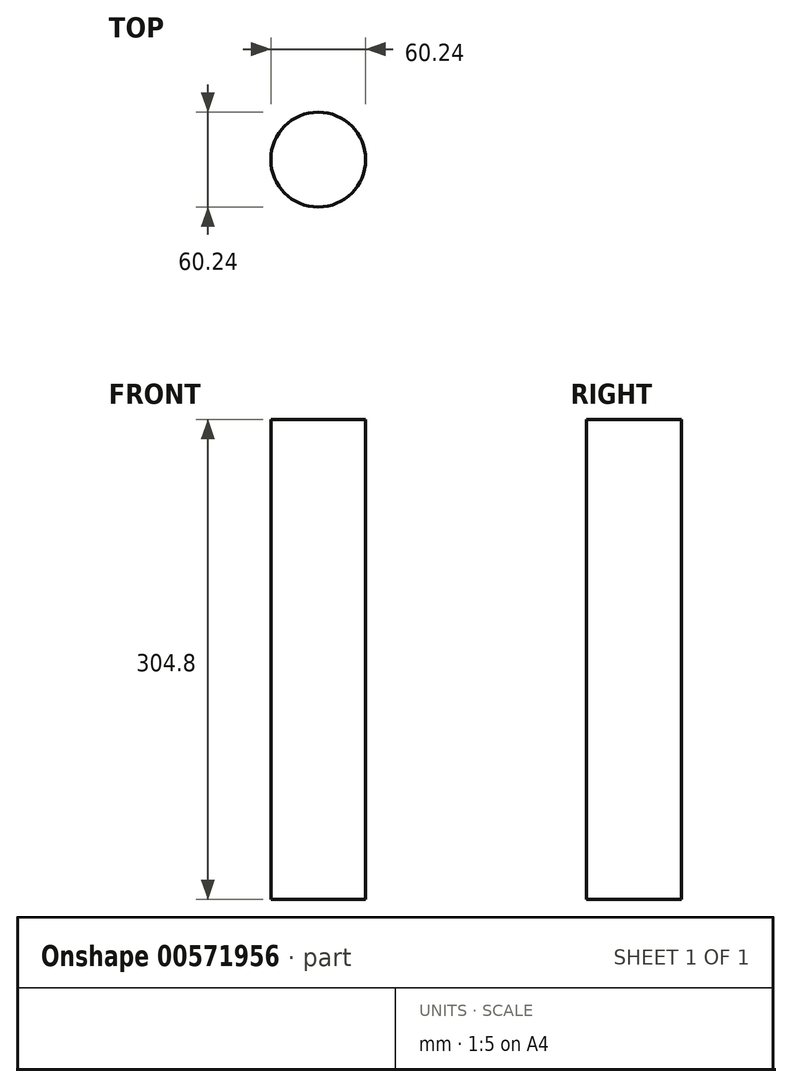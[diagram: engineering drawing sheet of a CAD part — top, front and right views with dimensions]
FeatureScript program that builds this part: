
annotation { "Feature Type Name" : "Feature", "Feature Type Description" : "" }
export const myFeature = defineFeature(function(context is Context, id is Id, definition is map)
    precondition{}
    {
        {
            var Q0;
            Q0=qCreatedBy(makeId("Top.planeOp"),FACE);
            var sketch = newSketch(context, id + "F0", { "sketchPlane" : qUnion([Q0])});
            skCircle(sketch, "E0", {"center": v(0, 0) * mm, "radius": 30.12 * mm});
            skSolve(sketch);
        }
        {
            var Q0;
            Q0 = qSketchRegion(id + "F0", true);
            extrude(context, id + "F1", {"entities" : qUnion([Q0]), "depth" : 304.8 * mm, "offsetDistance" : 25.4 * mm});
        }
    });
